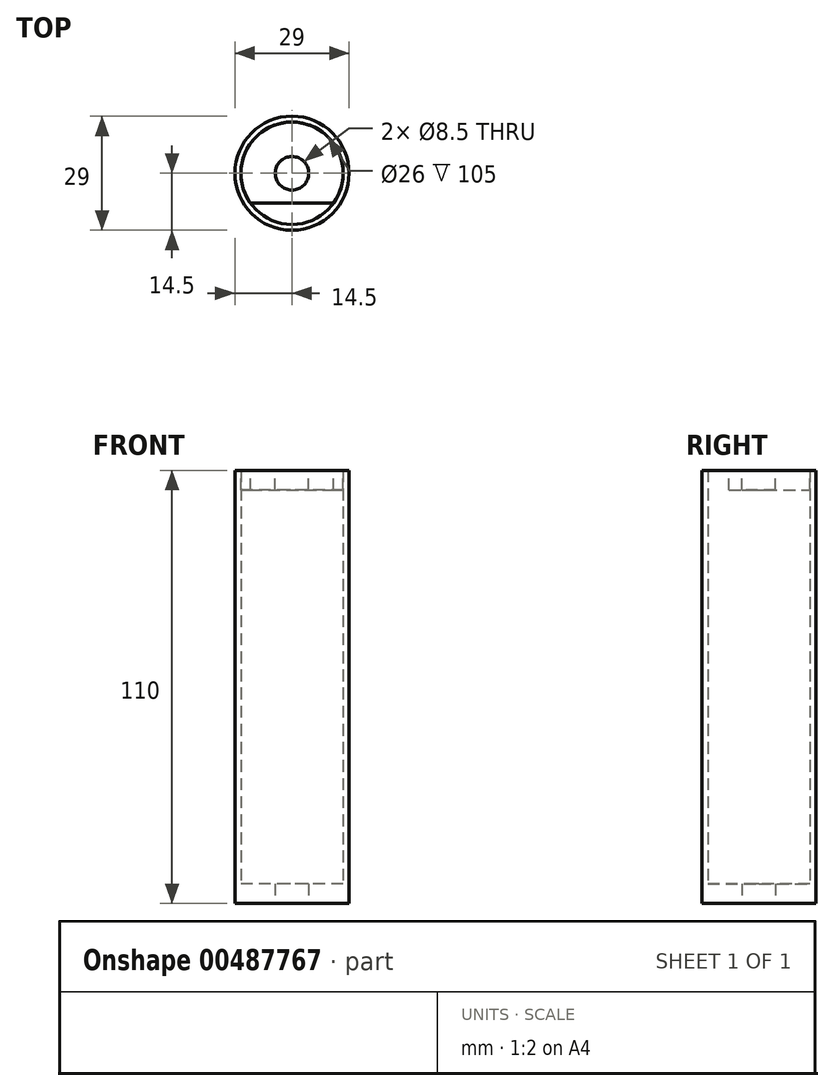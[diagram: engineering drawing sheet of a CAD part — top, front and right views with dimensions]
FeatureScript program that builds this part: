
annotation { "Feature Type Name" : "Feature", "Feature Type Description" : "" }
export const myFeature = defineFeature(function(context is Context, id is Id, definition is map)
    precondition{}
    {
        {
            var Q0;
            Q0=qCreatedBy(makeId("Top.planeOp"),FACE);
            var sketch = newSketch(context, id + "F0", { "sketchPlane" : qUnion([Q0])});
            skCircle(sketch, "E0", {"center": v(0, 0) * mm, "radius": 14.5 * mm});
            skSolve(sketch);
        }
        {
            var Q0;
            Q0 = qSketchRegion(id + "F0", true);
            extrude(context, id + "F1", {"entities" : qUnion([Q0]), "depth" : 5 * mm});
        }
        {
            var Q0;
            Q0=makeQuery(id+"F1.opExtrude","CAP_FACE",FACE,{"disambiguationData":[OSD([sQuery(id+"F0.wireOp",EDGE,"E0")])],"isStart":false});
            var sketch = newSketch(context, id + "F2", { "sketchPlane" : qUnion([Q0])});
            skCircle(sketch, "E1", {"center": v(0, 0) * mm, "radius": 13 * mm});
            skSolve(sketch);
        }
        {
            var Q0;
            Q0=makeQuery(id+"F2.imprint","IMPRINT",FACE,{"disambiguationData":[TD([[makeQuery(id+"F2.imprint","IMPRINT",EDGE,{"derivedFrom":sQuery(id+"F2.wireOp",EDGE,"E1")}),-1.0]])]});
            extrude(context, id + "F3", {"entities" : qUnion([Q0]), "operationType" : NewBodyOperationType.ADD, "depth" : 105 * mm});
        }
        {
            var Q0;
            Q0=makeQuery(id+"F1.opExtrude","CAP_FACE",FACE,{"disambiguationData":[OSD([sQuery(id+"F0.wireOp",EDGE,"E0")])],"isStart":true});
            var sketch = newSketch(context, id + "F4", { "sketchPlane" : qUnion([Q0])});
            skCircle(sketch, "E2", {"center": v(0, 0) * mm, "radius": 4.25 * mm});
            skSolve(sketch);
        }
        {
            var Q0;
            Q0 = qSketchRegion(id + "F4", true);
            var Q1;
            Q1=makeQuery(id+"F1.opExtrude","CAP_FACE",FACE,{"disambiguationData":[OSD([sQuery(id+"F0.wireOp",EDGE,"E0")])],"isStart":false});
            extrude(context, id + "F5", {"entities" : qUnion([Q0]), "operationType" : NewBodyOperationType.REMOVE, "endBound" : BoundingType.UP_TO_SURFACE, "oppositeDirection" : true, "endBoundEntityFace" : qUnion([Q1]), "depth" : 25 * mm});
        }
        {
            var Q0;
            Q0=makeQuery(id+"F3.opExtrude","CAP_FACE",FACE,{"disambiguationData":[OSD([sQuery(id+"F0.wireOp",EDGE,"E0"),sQuery(id+"F2.wireOp",EDGE,"E1")])],"isStart":false});
            var sketch = newSketch(context, id + "F6", { "sketchPlane" : qUnion([Q0])});
            skCircle(sketch, "E3", {"center": v(0, 0) * mm, "radius": 14.5 * mm});
            skLineSegment(sketch, "E4", {"start": v(-12.37, -7.56) * mm, "end": v(12.37, -7.56) * mm});
            skPoint(sketch, "E5.start.orphan", {"position": v(0, 14.5) * mm});
            skCircle(sketch, "E6", {"center": v(0, 0) * mm, "radius": 4.25 * mm});
            skSolve(sketch);
        }
        {
            var Q0;
            Q0=makeQuery(id+"F6.imprint","IMPRINT",FACE,{"disambiguationData":[TD([[makeQuery(id+"F6.imprint","IMPRINT",EDGE,{"derivedFrom":sQuery(id+"F6.wireOp",EDGE,"E6")}),-1.0]])]});
            extrude(context, id + "F7", {"entities" : qUnion([Q0]), "oppositeDirection" : true, "depth" : 5 * mm});
        }
    });
